# Revit family: Plumbing_FIxtures-Oasis-Drinking_Fountain_Contactless_Single
name_source: partatom
category: Plumbing Fixtures
units: mm (PartAtom-declared; Revit-internal decimal feet)

## family parameters
Cut with Voids When Loaded = No
Host = Face
OmniClass Number = 23.65.70.14.11
OmniClass Title = Drinking Fountains/Coolers
Part Type = Normal
Room Calculation Point = No
Round Connector Dimension = Use Diameter
Shared = No

## types (8) — shared parameters
Accessory Material = Plastic - Oasis International - Gray
Assembly Code = D2010800
Cold Water Connection Diameter = 0"
Default Elevation = 1' - 1 9/32"
Depth = 1' - 6 5/8"
Description = Refrigerated Fountain
Flow Rate = 8 GPH
Frequency = 60 Hz
HW Connection = No
Height = 1' - 6 7/8"
Instruction Sheet Link = https://www.oasiscoolers.com
Keynote = 22 40 00.A1
Load Classification = Power
Manufacturer = OASIS International
Manufacturer Fax Number = 1-(614) 322-2529
Product Documentation Link = https://www.oasiscoolers.com
Product Page URL = https://www.oasiscoolers.com
URL = https://www.oasiscoolers.com
Vent Connection = No
Version = 2021 - v1.0a
Voltage = 115 V
Voltage Comment = 115 Volts, 60 Hz
Waste Water Connection Diameter = 0' - 1 1/4"
Water Pressure = 60.00 psi
Water Pressure Range = 20 - 100 PSI
Weight = 64.00 lb
Width = 1' - 5 5/8"

## per-type parameters (varying)
| type | Cabinet Finish | Chilling Option | Filter Option | Finish | Full Load Current | Model | Product Name | Rated Watts | Warranty URL |
| PG8ACT-GRY | Paint - Oasis International - Greystone Powder Coated | Delivers 8.0 gallons of chilled drinking water per hour with touch free sensor | Option to add Filtration | Metal - Oasis International - Brushed Stainless Steel | 5 A | PG8ACT 506672 | Contactless Versacooler II, Refrigerated | 460 W |  |
| PGF8ACT-GRY | Paint - Oasis International - Greystone Powder Coated | Delivers 8.0 gallons of chilled drinking water per hour with VersaFilter and contactless sensor | VersaFilter for taste, odor, lead and chlorine reduction | Metal - Oasis International - Brushed Stainless Steel | 4 A | PGF8ACT 506675 | Filtered Contactless Versacooler II, Refrigerated | 440 W | https://www.oasiscoolers.com |
| PGF8ACT-SAN | Metal - Oasis International - Steel Painted Sandstone | Delivers 8.0 gallons of chilled drinking water per hour with VersaFilter and contactless sensor | VersaFilter for taste, odor, lead and chlorine reduction | Metal - Oasis International - Brushed Stainless Steel | 4 A | PGF8ACT 506032 | Filtered Contactless Versacooler II, Refrigerated | 440 W | https://www.oasiscoolers.com |
| PGF8ACT-STL | Metal - Oasis International - Brushed Stainless Steel | Delivers 8.0 gallons of chilled drinking water per hour with VersaFilter and contactless sensor | VersaFilter for taste, odor, lead and chlorine reduction | Metal - Oasis International - Brushed Stainless Steel | 4 A | PGF8ACT 506033 | Filtered Contactless Versacooler II, Refrigerated | 440 W | https://www.oasiscoolers.com |
| PGF8ACT-CHR | Metal - Oasis International - Chrome Plated Brass | Delivers 8.0 gallons of chilled drinking water per hour with VersaFilter and contactless sensor | VersaFilter for taste, odor, lead and chlorine reduction | Metal - Oasis International - Chrome Plated Brass | 4 A | PGF8ACT 036700-001 | Filtered Contactless Versacooler II, Refrigerated | 440 W | https://www.oasiscoolers.com |
| PG8ACT-SAN | Metal - Oasis International - Steel Painted Sandstone | Delivers 8.0 gallons of chilled drinking water per hour with touch free sensor | Option to add Filtration | Metal - Oasis International - Brushed Stainless Steel | 5 A | PG8ACT 506028 | Contactless Versacooler II, Refrigerated | 460 W |  |
| PG8ACT-STL | Metal - Oasis International - Brushed Stainless Steel | Delivers 8.0 gallons of chilled drinking water per hour with touch free sensor | Option to add Filtration | Metal - Oasis International - Brushed Stainless Steel | 5 A | PG8ACT 506029 | Contactless Versacooler II, Refrigerated | 460 W |  |
| PG8ACT-CHR | Metal - Oasis International - Chrome Plated Brass | Delivers 8.0 gallons of chilled drinking water per hour with touch free sensor | Option to add Filtration | Metal - Oasis International - Chrome Plated Brass | 5 A | PG8ACT 036700-001 | Contactless Versacooler II, Refrigerated | 460 W |  |

## geometry (parser evidence)
native form markers: Sweep x2
no freeform markers — native parametric forms only
